# Revit family: Faucet-Lavatory-KOHLER-July-K-16027-4
name_source: partatom
category: Plumbing Fixtures
revit_build: Autodesk Revit 2015 (Build: 20140606_1530(x64)
units: mm (PartAtom-declared; Revit-internal decimal feet)

## types (2) — shared parameters
ADA Compliant = Yes
Assembly Code = D2010900
CW Connection = Yes
Date Modified = 09/17/2017
Default Elevation = 36"
Description = July Single-handle bathroom sink faucet
Flow Rate = 1 GPM
HW Connection = Yes
Height = 4 9/16"
Length = 1 29/32"
Manufacturer = Kohler
MasterFormat 1995 = 15410
MasterFormat 2004 = 22.41.39
Material = Brass Construction
Pressure = 60.00 psi
Product Documentation Link = http://www.us.kohler.com
Product Name = July
Product Page URL = http://www.us.kohler.com
Spout Reach = 4 1/16"
URL = http://www.us.kohler.com
Width = 5 11/16"

## per-type parameters (varying)
| type | Finish | Model | Type |
| CP-Polished Chrome | Metal-Kohler-CP-Polished Chrome | K-16027-4-CP | 1 |
| G-Brushed Chrome | Metal-Kohler-G-Brushed Chrome | K-16027-4-G | 2 |

## geometry (parser evidence)
native form markers: Blend x4, Sweep x4
no freeform markers — native parametric forms only
